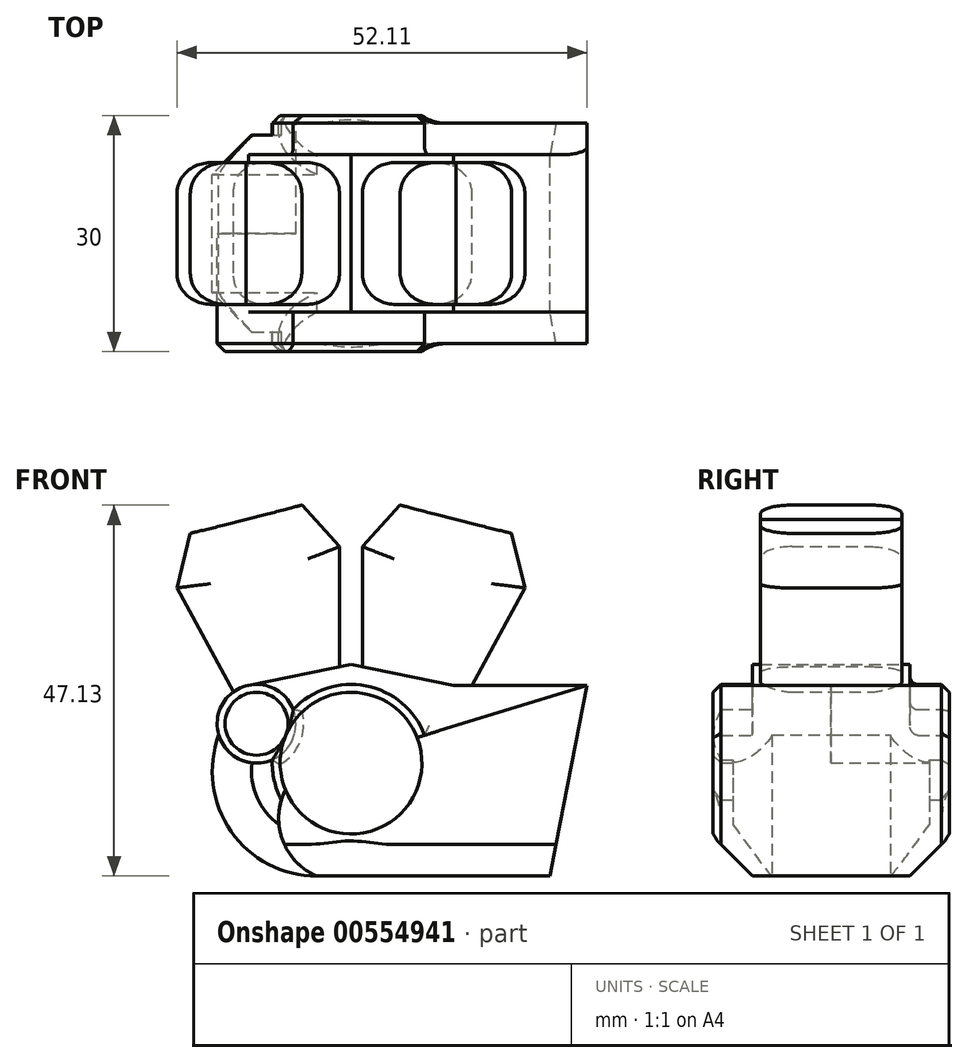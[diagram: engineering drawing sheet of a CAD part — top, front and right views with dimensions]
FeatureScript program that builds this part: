
annotation { "Feature Type Name" : "Feature", "Feature Type Description" : "" }
export const myFeature = defineFeature(function(context is Context, id is Id, definition is map)
    precondition{}
    {
        {
            var Q0;
            Q0=qCreatedBy(makeId("Front.planeOp"),FACE);
            var sketch = newSketch(context, id + "F0", { "sketchPlane" : qUnion([Q0])});
            skCircle(sketch, "E0", {"center": v(-30, 20) * mm, "radius": 10 * mm});
            skCircle(sketch, "E1", {"center": v(-42, 25) * mm, "radius": 5 * mm});
            skLineSegment(sketch, "E2", {"start": v(-30, 20) * mm, "end": v(-30, 32.55) * mm, "construction": true});
            skLineSegment(sketch, "E3", {"start": v(-43, 29.9) * mm, "end": v(-30, 32.55) * mm});
            skLineSegment(sketch, "E4", {"start": v(-30, 32.55) * mm, "end": v(-30, 32.55) * mm});
            skLineSegment(sketch, "E5.MirrorCS", {"start": v(-17, 29.9) * mm, "end": v(-30, 32.55) * mm});
            skLineSegment(sketch, "E6", {"start": v(-17, 29.9) * mm, "end": v(-17, 29.9) * mm});
            skLineSegment(sketch, "E7", {"start": v(-17, 29.9) * mm, "end": v(0, 29.9) * mm});
            skLineSegment(sketch, "E8", {"start": v(0, 29.9) * mm, "end": v(-20.65, 23.54) * mm});
            skArc(sketch, "E9", {"start": v(-38.84, 15.33) * mm, "mid": v(-38.44, 9.63) * mm, "end": v(-34.34, 5.65) * mm});
            skLineSegment(sketch, "E10", {"start": v(-34.34, 5.65) * mm, "end": v(-4.71, 5.65) * mm});
            skLineSegment(sketch, "E11", {"start": v(-4.71, 5.65) * mm, "end": v(0, 29.9) * mm});
            skLineSegment(sketch, "E12", {"start": v(-41.78, 44.87) * mm, "end": v(-52.1, 42.25) * mm});
            skLineSegment(sketch, "E13", {"start": v(-43.32, 50.92) * mm, "end": v(-50.42, 49.18) * mm});
            skLineSegment(sketch, "E14", {"start": v(-50.42, 49.18) * mm, "end": v(-52.1, 42.25) * mm});
            skLineSegment(sketch, "E15", {"start": v(-38.22, 30.87) * mm, "end": v(-43.7, 52.47) * mm, "construction": true});
            skLineSegment(sketch, "E16.MirrorCS", {"start": v(-43.32, 50.92) * mm, "end": v(-36.24, 52.78) * mm});
            skLineSegment(sketch, "E17.MirrorCS", {"start": v(-36.24, 52.78) * mm, "end": v(-31.45, 47.5) * mm});
            skLineSegment(sketch, "E18.MirrorCS", {"start": v(-41.78, 44.87) * mm, "end": v(-31.45, 47.5) * mm});
            skLineSegment(sketch, "E19.MirrorCS", {"start": v(-18.22, 44.87) * mm, "end": v(-7.9, 42.25) * mm});
            skLineSegment(sketch, "E20.MirrorCS", {"start": v(-18.22, 44.87) * mm, "end": v(-28.55, 47.5) * mm});
            skLineSegment(sketch, "E21.MirrorCS", {"start": v(-16.68, 50.92) * mm, "end": v(-23.76, 52.78) * mm});
            skLineSegment(sketch, "E22.MirrorCS", {"start": v(-16.68, 50.92) * mm, "end": v(-9.58, 49.18) * mm});
            skLineSegment(sketch, "E23.MirrorCS", {"start": v(-9.58, 49.18) * mm, "end": v(-7.9, 42.25) * mm});
            skLineSegment(sketch, "E24.MirrorCS", {"start": v(-23.76, 52.78) * mm, "end": v(-28.55, 47.5) * mm});
            skLineSegment(sketch, "E25.MirrorCS", {"start": v(-21.78, 30.87) * mm, "end": v(-16.3, 52.47) * mm, "construction": true});
            skPoint(sketch, "E26.MirrorCS.start.orphan", {"position": v(-28.55, 47.5) * mm});
            skLineSegment(sketch, "E27", {"start": v(-31.45, 47.5) * mm, "end": v(-31.45, 32.26) * mm});
            skLineSegment(sketch, "E28", {"start": v(-28.55, 47.5) * mm, "end": v(-28.55, 32.26) * mm});
            skLineSegment(sketch, "E29.MirrorCS", {"start": v(-52.1, 42.25) * mm, "end": v(-44.94, 29.05) * mm});
            skLineSegment(sketch, "E30.MirrorCS", {"start": v(-7.9, 42.25) * mm, "end": v(-14.6, 29.9) * mm});
            skPoint(sketch, "E31.orphan", {"position": v(-44.83, 28.86) * mm});
            skPoint(sketch, "E32.orphan", {"position": v(-15.17, 28.86) * mm});
            skPoint(sketch, "E33.MirrorCS.end.orphan", {"position": v(-17, 29.9) * mm});
            skPoint(sketch, "E33.MirrorCS.start.orphan", {"position": v(-7.9, 42.25) * mm});
            skArc(sketch, "E34", {"start": v(-46.8, 23.57) * mm, "mid": v(-45.25, 11.35) * mm, "end": v(-34.34, 5.65) * mm});
            skSolve(sketch);
        }
        {
            var Q0;
            {var subQ0=sQuery(id+"F0.wireOp",EDGE,"E0");var subQ1=makeQuery(id+"F0.imprint","INTERSECT",VERTEX,{"derivedFrom":[subQ0,sQuery(id+"F0.wireOp",EDGE,"E8")]});Q0=makeQuery(id+"F0.imprint","IMPRINT",FACE,{"disambiguationData":[TD([[makeQuery(id+"F0.imprint","IMPRINT",EDGE,{"disambiguationData":[TD([[subQ1,-1.0]])],"derivedFrom":subQ0}),1.0]])]});}
            extrude(context, id + "F1", {"entities" : qUnion([Q0]), "endBound" : BoundingType.SYMMETRIC, "depth" : 30 * mm, "offsetDistance" : 25 * mm});
        }
        {
            var Q0;
            {var subQ0=sQuery(id+"F0.wireOp",EDGE,"E1");var subQ3=sQuery(id+"F0.wireOp",EDGE,"E0");var subQ4=makeQuery(id+"F0.imprint","INTERSECT",VERTEX,{"disambiguationData":[OD(0.0)],"derivedFrom":[subQ3,subQ0]});Q0=makeQuery(id+"F0.imprint","IMPRINT",FACE,{"disambiguationData":[TD([[makeQuery(id+"F0.imprint","IMPRINT",EDGE,{"disambiguationData":[TD([[subQ4,-1.0]])],"derivedFrom":subQ3}),-1.0]])]});}
            var Q1;
            {var subQ0=sQuery(id+"F0.wireOp",EDGE,"E1");var subQ1=sQuery(id+"F0.wireOp",EDGE,"E0");var subQ2=makeQuery(id+"F0.imprint","INTERSECT",VERTEX,{"disambiguationData":[OD(0.0)],"derivedFrom":[subQ1,subQ0]});Q1=makeQuery(id+"F0.imprint","IMPRINT",FACE,{"disambiguationData":[TD([[makeQuery(id+"F0.imprint","IMPRINT",EDGE,{"disambiguationData":[TD([[subQ2,-1.0]])],"derivedFrom":subQ1}),1.0]])]});}
            extrude(context, id + "F2", {"entities" : qUnion([Q0, Q1]), "operationType" : NewBodyOperationType.ADD, "depth" : 15 * mm, "offsetDistance" : 25 * mm});
        }
        {
            var Q0;
            Q0=makeQuery(id+"F1.opExtrude","CAP_EDGE",EDGE,{"disambiguationData":[OSD([sQuery(id+"F0.wireOp",EDGE,"E0")])],"isStart":false});
            var Q1;
            Q1=makeQuery(id+"F1.opExtrude","CAP_EDGE",EDGE,{"disambiguationData":[OSD([sQuery(id+"F0.wireOp",EDGE,"E0")])],"isStart":true});
            var Q2;
            Q2=makeQuery(id+"F2.opExtrude","CAP_EDGE",EDGE,{"disambiguationData":[OSD([sQuery(id+"F0.wireOp",EDGE,"E1")])],"isStart":false});
            var Q3;
            Q3=makeQuery(id+"F1.opExtrude","CAP_EDGE",EDGE,{"disambiguationData":[OSD([sQuery(id+"F0.wireOp",EDGE,"E1")])],"isStart":true});
            chamfer(context, id + "F3", {"entities" : qUnion([Q0, Q1, Q2, Q3]), "width" : 1 * mm, "tangentPropagation" : true});
        }
        {
            var Q0;
            {var subQ0=sQuery(id+"F0.wireOp",EDGE,"E9");Q0=makeQuery(id+"F0.imprint","IMPRINT",FACE,{"disambiguationData":[TD([[makeQuery(id+"F0.imprint","IMPRINT",EDGE,{"derivedFrom":subQ0}),-1.0]])]});}
            extrude(context, id + "F4", {"entities" : qUnion([Q0]), "operationType" : NewBodyOperationType.ADD, "endBound" : BoundingType.SYMMETRIC, "depth" : 25 * mm, "offsetDistance" : 25 * mm});
        }
        {
            var Q0;
            {var subQ1=sQuery(id+"F0.wireOp",EDGE,"E8");Q0=makeQuery(id+"F0.imprint","IMPRINT",FACE,{"disambiguationData":[TD([[makeQuery(id+"F0.imprint","IMPRINT",EDGE,{"derivedFrom":subQ1}),1.0]])]});}
            extrude(context, id + "F5", {"entities" : qUnion([Q0]), "operationType" : NewBodyOperationType.ADD, "endBound" : BoundingType.SYMMETRIC, "depth" : 28 * mm, "offsetDistance" : 25 * mm});
        }
        {
            var Q0;
            Q0=makeQuery(id+"F4.opExtrude","CAP_EDGE",EDGE,{"disambiguationData":[OSD([sQuery(id+"F0.wireOp",EDGE,"E34")])],"isStart":false});
            var Q1;
            Q1=makeQuery(id+"F4.opExtrude","CAP_EDGE",EDGE,{"disambiguationData":[OSD([sQuery(id+"F0.wireOp",EDGE,"E34")])],"isStart":true});
            chamfer(context, id + "F6", {"entities" : qUnion([Q0, Q1]), "width" : 5 * mm, "tangentPropagation" : true});
        }
        {
            var Q0;
            Q0=makeQuery(id+"F5.opExtrude","CAP_EDGE",EDGE,{"disambiguationData":[OSD([sQuery(id+"F0.wireOp",EDGE,"E10")])],"isStart":true});
            var Q1;
            Q1=makeQuery(id+"F5.opExtrude","CAP_EDGE",EDGE,{"disambiguationData":[OSD([sQuery(id+"F0.wireOp",EDGE,"E10")])],"isStart":false});
            chamfer(context, id + "F7", {"entities" : qUnion([Q0, Q1]), "width" : 4 * mm, "tangentPropagation" : true});
        }
        {
            var Q0;
            {var subQ0=sQuery(id+"F0.wireOp",EDGE,"E0");Q0=makeQuery(id+"F5.boolean.opBoolean","MERGE",EDGE,{"derivedFrom":[makeQuery(id+"F3.opChamfer","BLEND_EDGE",EDGE,{"blendedFrom":[makeQuery(id+"F1.opExtrude","CAP_EDGE",EDGE,{"disambiguationData":[OSD([subQ0])],"isStart":false}),makeQuery(id+"F1.opExtrude","SWEPT_FACE",FACE,{"disambiguationData":[OSD([subQ0])]})],"blendedInto":[makeQuery(id+"F1.opExtrude","SWEPT_FACE",FACE,{"disambiguationData":[OSD([subQ0])]})]}),makeQuery(id+"F5.opExtrude","CAP_EDGE",EDGE,{"disambiguationData":[OSD([subQ0])],"isStart":false})]});}
            var Q1;
            {var subQ0=sQuery(id+"F0.wireOp",EDGE,"E0");Q1=makeQuery(id+"F5.boolean.opBoolean","MERGE",EDGE,{"derivedFrom":[makeQuery(id+"F3.opChamfer","BLEND_EDGE",EDGE,{"blendedFrom":[makeQuery(id+"F1.opExtrude","CAP_EDGE",EDGE,{"disambiguationData":[OSD([subQ0])],"isStart":true}),makeQuery(id+"F1.opExtrude","SWEPT_FACE",FACE,{"disambiguationData":[OSD([subQ0])]})],"blendedInto":[makeQuery(id+"F1.opExtrude","SWEPT_FACE",FACE,{"disambiguationData":[OSD([subQ0])]})]}),makeQuery(id+"F5.opExtrude","CAP_EDGE",EDGE,{"disambiguationData":[OSD([subQ0])],"isStart":true})]});}
            fillet(context, id + "F8", {"entities" : qUnion([Q0, Q1]), "radius" : 5 * mm, "tangentPropagation" : true, "allowEdgeOverflow" : false});
        }
        {
            var Q0;
            {var subQ6=sQuery(id+"F0.wireOp",EDGE,"E8");Q0=makeQuery(id+"F0.imprint","IMPRINT",FACE,{"disambiguationData":[TD([[makeQuery(id+"F0.imprint","IMPRINT",EDGE,{"derivedFrom":subQ6}),-1.0]])]});}
            extrude(context, id + "F9", {"entities" : qUnion([Q0]), "operationType" : NewBodyOperationType.ADD, "endBound" : BoundingType.SYMMETRIC, "depth" : 20 * mm, "offsetDistance" : 25 * mm});
        }
        {
            var Q0;
            Q0=makeQuery(id+"F9.opExtrude","CAP_EDGE",EDGE,{"disambiguationData":[OSD([sQuery(id+"F0.wireOp",EDGE,"E8")])],"isStart":false});
            var Q1;
            Q1=makeQuery(id+"F9.opExtrude","CAP_EDGE",EDGE,{"disambiguationData":[OSD([sQuery(id+"F0.wireOp",EDGE,"E0")])],"isStart":false});
            var Q2;
            Q2=makeQuery(id+"F9.opExtrude","CAP_EDGE",EDGE,{"disambiguationData":[OSD([sQuery(id+"F0.wireOp",EDGE,"E1")])],"isStart":false});
            var Q3;
            Q3=makeQuery(id+"F9.opExtrude","CAP_EDGE",EDGE,{"disambiguationData":[OSD([sQuery(id+"F0.wireOp",EDGE,"E0")])],"isStart":true});
            var Q4;
            Q4=makeQuery(id+"F9.opExtrude","CAP_EDGE",EDGE,{"disambiguationData":[OSD([sQuery(id+"F0.wireOp",EDGE,"E8")])],"isStart":true});
            fillet(context, id + "F10", {"entities" : qUnion([Q0, Q1, Q2, Q3, Q4]), "radius" : 1 * mm, "tangentPropagation" : true, "allowEdgeOverflow" : false});
        }
        {
            var Q0;
            Q0=makeQuery(id+"F0.imprint","IMPRINT",FACE,{"disambiguationData":[TD([[makeQuery(id+"F0.imprint","IMPRINT",EDGE,{"derivedFrom":sQuery(id+"F0.wireOp",EDGE,"E19.MirrorCS")}),-1.0]])]});
            var Q1;
            Q1=makeQuery(id+"F0.imprint","IMPRINT",FACE,{"disambiguationData":[TD([[makeQuery(id+"F0.imprint","IMPRINT",EDGE,{"derivedFrom":sQuery(id+"F0.wireOp",EDGE,"E19.MirrorCS")}),1.0]])]});
            var Q2;
            Q2=makeQuery(id+"F0.imprint","IMPRINT",FACE,{"disambiguationData":[TD([[makeQuery(id+"F0.imprint","IMPRINT",EDGE,{"derivedFrom":sQuery(id+"F0.wireOp",EDGE,"E12")}),-1.0]])]});
            var Q3;
            Q3=makeQuery(id+"F0.imprint","IMPRINT",FACE,{"disambiguationData":[TD([[makeQuery(id+"F0.imprint","IMPRINT",EDGE,{"derivedFrom":sQuery(id+"F0.wireOp",EDGE,"E12")}),1.0]])]});
            extrude(context, id + "F11", {"entities" : qUnion([Q0, Q1, Q2, Q3]), "operationType" : NewBodyOperationType.ADD, "endBound" : BoundingType.SYMMETRIC, "depth" : 18 * mm, "offsetDistance" : 25 * mm});
        }
        {
            var Q0;
            Q0=makeQuery(id+"F11.opExtrude","CAP_EDGE",EDGE,{"disambiguationData":[OSD([sQuery(id+"F0.wireOp",EDGE,"E14")])],"isStart":false});
            var Q1;
            Q1=makeQuery(id+"F11.opExtrude","CAP_EDGE",EDGE,{"disambiguationData":[OSD([sQuery(id+"F0.wireOp",EDGE,"E29.MirrorCS")])],"isStart":false});
            var Q2;
            Q2=makeQuery(id+"F11.opExtrude","CAP_EDGE",EDGE,{"disambiguationData":[OSD([sQuery(id+"F0.wireOp",EDGE,"E29.MirrorCS")])],"isStart":true});
            var Q3;
            Q3=makeQuery(id+"F11.opExtrude","CAP_EDGE",EDGE,{"disambiguationData":[OSD([sQuery(id+"F0.wireOp",EDGE,"E14")])],"isStart":true});
            var Q4;
            Q4=makeQuery(id+"F11.opExtrude","CAP_EDGE",EDGE,{"disambiguationData":[OSD([sQuery(id+"F0.wireOp",EDGE,"E28")])],"isStart":false});
            var Q5;
            Q5=makeQuery(id+"F11.opExtrude","CAP_EDGE",EDGE,{"disambiguationData":[OSD([sQuery(id+"F0.wireOp",EDGE,"E27")])],"isStart":false});
            var Q6;
            Q6=makeQuery(id+"F11.opExtrude","CAP_EDGE",EDGE,{"disambiguationData":[OSD([sQuery(id+"F0.wireOp",EDGE,"E17.MirrorCS")])],"isStart":false});
            var Q7;
            Q7=makeQuery(id+"F11.opExtrude","CAP_EDGE",EDGE,{"disambiguationData":[OSD([sQuery(id+"F0.wireOp",EDGE,"E24.MirrorCS")])],"isStart":false});
            var Q8;
            Q8=makeQuery(id+"F11.opExtrude","CAP_EDGE",EDGE,{"disambiguationData":[OSD([sQuery(id+"F0.wireOp",EDGE,"E23.MirrorCS")])],"isStart":false});
            var Q9;
            Q9=makeQuery(id+"F11.opExtrude","CAP_EDGE",EDGE,{"disambiguationData":[OSD([sQuery(id+"F0.wireOp",EDGE,"E30.MirrorCS")])],"isStart":false});
            var Q10;
            Q10=makeQuery(id+"F11.opExtrude","CAP_EDGE",EDGE,{"disambiguationData":[OSD([sQuery(id+"F0.wireOp",EDGE,"E30.MirrorCS")])],"isStart":true});
            var Q11;
            Q11=makeQuery(id+"F11.opExtrude","CAP_EDGE",EDGE,{"disambiguationData":[OSD([sQuery(id+"F0.wireOp",EDGE,"E23.MirrorCS")])],"isStart":true});
            var Q12;
            Q12=makeQuery(id+"F11.opExtrude","CAP_EDGE",EDGE,{"disambiguationData":[OSD([sQuery(id+"F0.wireOp",EDGE,"E24.MirrorCS")])],"isStart":true});
            var Q13;
            Q13=makeQuery(id+"F11.opExtrude","CAP_EDGE",EDGE,{"disambiguationData":[OSD([sQuery(id+"F0.wireOp",EDGE,"E28")])],"isStart":true});
            var Q14;
            Q14=makeQuery(id+"F11.opExtrude","CAP_EDGE",EDGE,{"disambiguationData":[OSD([sQuery(id+"F0.wireOp",EDGE,"E27")])],"isStart":true});
            var Q15;
            Q15=makeQuery(id+"F11.opExtrude","CAP_EDGE",EDGE,{"disambiguationData":[OSD([sQuery(id+"F0.wireOp",EDGE,"E17.MirrorCS")])],"isStart":true});
            fillet(context, id + "F12", {"entities" : qUnion([Q0, Q1, Q2, Q3, Q4, Q5, Q6, Q7, Q8, Q9, Q10, Q11, Q12, Q13, Q14, Q15]), "radius" : 4 * mm, "tangentPropagation" : true, "allowEdgeOverflow" : false});
        }
    });
